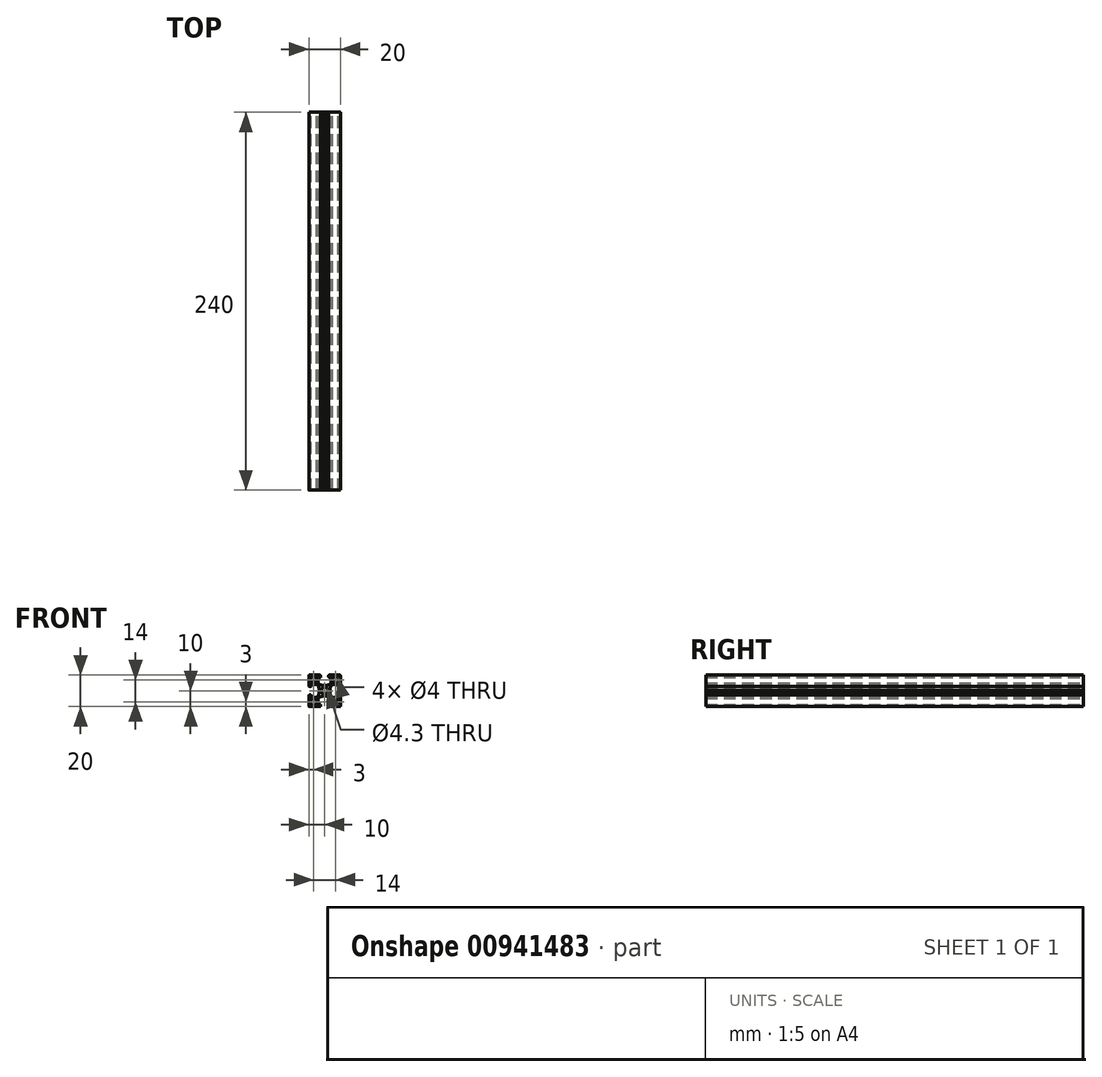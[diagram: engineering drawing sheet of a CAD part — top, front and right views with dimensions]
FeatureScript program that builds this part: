
annotation { "Feature Type Name" : "Feature", "Feature Type Description" : "" }
export const myFeature = defineFeature(function(context is Context, id is Id, definition is map)
    precondition{}
    {
        {
            var Q0;
            Q0=qCreatedBy(makeId("Front.planeOp"),FACE);
            var sketch = newSketch(context, id + "F0", { "sketchPlane" : qUnion([Q0])});
            skLineSegment(sketch, "E0", {"start": v(-11.2, 0) * mm, "end": v(11.2, 0) * mm});
            skCircle(sketch, "E1", {"center": v(0, 0) * mm, "radius": 2.15 * mm});
            skLineSegment(sketch, "E2", {"start": v(4.15, 4.94) * mm, "end": v(4.15, 8.2) * mm});
            skArc(sketch, "E3", {"start": v(4.15, 8.2) * mm, "mid": v(4.06, 8.41) * mm, "end": v(3.85, 8.5) * mm});
            skLineSegment(sketch, "E4", {"start": v(3.85, 8.5) * mm, "end": v(2.95, 8.5) * mm});
            skArc(sketch, "E5", {"start": v(2.95, 8.5) * mm, "mid": v(2.74, 8.59) * mm, "end": v(2.65, 8.8) * mm});
            skLineSegment(sketch, "E6", {"start": v(2.65, 8.8) * mm, "end": v(2.65, 9.7) * mm});
            skArc(sketch, "E7", {"start": v(2.65, 9.7) * mm, "mid": v(2.74, 9.91) * mm, "end": v(2.95, 10) * mm});
            skLineSegment(sketch, "E8", {"start": v(2.95, 10) * mm, "end": v(9.7, 10) * mm});
            skArc(sketch, "E9", {"start": v(9.7, 10) * mm, "mid": v(9.91, 9.91) * mm, "end": v(10, 9.7) * mm});
            skLineSegment(sketch, "E10", {"start": v(10, 9.7) * mm, "end": v(10, 2.95) * mm});
            skArc(sketch, "E11", {"start": v(10, 2.95) * mm, "mid": v(9.91, 2.74) * mm, "end": v(9.7, 2.65) * mm});
            skLineSegment(sketch, "E12", {"start": v(9.7, 2.65) * mm, "end": v(8.8, 2.65) * mm});
            skArc(sketch, "E13", {"start": v(8.8, 2.65) * mm, "mid": v(8.59, 2.74) * mm, "end": v(8.5, 2.95) * mm});
            skLineSegment(sketch, "E14", {"start": v(8.5, 2.95) * mm, "end": v(8.5, 3.85) * mm});
            skArc(sketch, "E15", {"start": v(8.5, 3.85) * mm, "mid": v(8.41, 4.06) * mm, "end": v(8.2, 4.15) * mm});
            skLineSegment(sketch, "E16", {"start": v(8.2, 4.15) * mm, "end": v(4.94, 4.15) * mm});
            skArc(sketch, "E17", {"start": v(4.94, 4.15) * mm, "mid": v(4.81, 4.12) * mm, "end": v(4.7, 4.04) * mm});
            skArc(sketch, "E18", {"start": v(4.7, 4.04) * mm, "mid": v(3.71, 2.28) * mm, "end": v(3.3, 0.3) * mm});
            skLineSegment(sketch, "E19", {"start": v(3.3, 0.3) * mm, "end": v(3, 0) * mm});
            skLineSegment(sketch, "E20", {"start": v(3, 0) * mm, "end": v(3.3, -0.3) * mm});
            skArc(sketch, "E21", {"start": v(3.3, -0.3) * mm, "mid": v(3.71, -2.28) * mm, "end": v(4.7, -4.04) * mm});
            skArc(sketch, "E22", {"start": v(4.7, -4.04) * mm, "mid": v(4.81, -4.12) * mm, "end": v(4.94, -4.15) * mm});
            skLineSegment(sketch, "E23", {"start": v(4.94, -4.15) * mm, "end": v(8.2, -4.15) * mm});
            skArc(sketch, "E24", {"start": v(8.2, -4.15) * mm, "mid": v(8.41, -4.06) * mm, "end": v(8.5, -3.85) * mm});
            skLineSegment(sketch, "E25", {"start": v(8.5, -3.85) * mm, "end": v(8.5, -2.95) * mm});
            skArc(sketch, "E26", {"start": v(8.5, -2.95) * mm, "mid": v(8.59, -2.74) * mm, "end": v(8.8, -2.65) * mm});
            skLineSegment(sketch, "E27", {"start": v(8.8, -2.65) * mm, "end": v(9.7, -2.65) * mm});
            skArc(sketch, "E28", {"start": v(9.7, -2.65) * mm, "mid": v(9.91, -2.74) * mm, "end": v(10, -2.95) * mm});
            skLineSegment(sketch, "E29", {"start": v(10, -2.95) * mm, "end": v(10, -9.7) * mm});
            skArc(sketch, "E30", {"start": v(10, -9.7) * mm, "mid": v(9.91, -9.91) * mm, "end": v(9.7, -10) * mm});
            skLineSegment(sketch, "E31", {"start": v(9.7, -10) * mm, "end": v(2.95, -10) * mm});
            skArc(sketch, "E32", {"start": v(2.95, -10) * mm, "mid": v(2.74, -9.91) * mm, "end": v(2.65, -9.7) * mm});
            skLineSegment(sketch, "E33", {"start": v(2.65, -9.7) * mm, "end": v(2.65, -8.8) * mm});
            skArc(sketch, "E34", {"start": v(2.65, -8.8) * mm, "mid": v(2.74, -8.59) * mm, "end": v(2.95, -8.5) * mm});
            skLineSegment(sketch, "E35", {"start": v(2.95, -8.5) * mm, "end": v(3.85, -8.5) * mm});
            skArc(sketch, "E36", {"start": v(3.85, -8.5) * mm, "mid": v(4.06, -8.41) * mm, "end": v(4.15, -8.2) * mm});
            skLineSegment(sketch, "E37", {"start": v(4.15, -8.2) * mm, "end": v(4.15, -4.94) * mm});
            skArc(sketch, "E38", {"start": v(4.15, -4.94) * mm, "mid": v(4.12, -4.81) * mm, "end": v(4.04, -4.7) * mm});
            skArc(sketch, "E39", {"start": v(4.04, -4.7) * mm, "mid": v(2.28, -3.71) * mm, "end": v(0.3, -3.3) * mm});
            skLineSegment(sketch, "E40", {"start": v(0.3, -3.3) * mm, "end": v(0, -3) * mm});
            skLineSegment(sketch, "E41", {"start": v(0, -3) * mm, "end": v(-0.3, -3.3) * mm});
            skArc(sketch, "E42", {"start": v(-0.3, -3.3) * mm, "mid": v(-2.28, -3.71) * mm, "end": v(-4.04, -4.7) * mm});
            skArc(sketch, "E43", {"start": v(-4.04, -4.7) * mm, "mid": v(-4.12, -4.81) * mm, "end": v(-4.15, -4.94) * mm});
            skLineSegment(sketch, "E44", {"start": v(-4.15, -4.94) * mm, "end": v(-4.15, -8.2) * mm});
            skArc(sketch, "E45", {"start": v(-4.15, -8.2) * mm, "mid": v(-4.06, -8.41) * mm, "end": v(-3.85, -8.5) * mm});
            skLineSegment(sketch, "E46", {"start": v(-3.85, -8.5) * mm, "end": v(-2.95, -8.5) * mm});
            skArc(sketch, "E47", {"start": v(-2.95, -8.5) * mm, "mid": v(-2.74, -8.59) * mm, "end": v(-2.65, -8.8) * mm});
            skLineSegment(sketch, "E48", {"start": v(-2.65, -8.8) * mm, "end": v(-2.65, -9.7) * mm});
            skArc(sketch, "E49", {"start": v(-2.65, -9.7) * mm, "mid": v(-2.74, -9.91) * mm, "end": v(-2.95, -10) * mm});
            skLineSegment(sketch, "E50", {"start": v(-2.95, -10) * mm, "end": v(-9.7, -10) * mm});
            skArc(sketch, "E51", {"start": v(-9.7, -10) * mm, "mid": v(-9.91, -9.91) * mm, "end": v(-10, -9.7) * mm});
            skLineSegment(sketch, "E52", {"start": v(-10, -9.7) * mm, "end": v(-10, -2.95) * mm});
            skArc(sketch, "E53", {"start": v(-10, -2.95) * mm, "mid": v(-9.91, -2.74) * mm, "end": v(-9.7, -2.65) * mm});
            skLineSegment(sketch, "E54", {"start": v(-9.7, -2.65) * mm, "end": v(-8.8, -2.65) * mm});
            skArc(sketch, "E55", {"start": v(-8.8, -2.65) * mm, "mid": v(-8.59, -2.74) * mm, "end": v(-8.5, -2.95) * mm});
            skLineSegment(sketch, "E56", {"start": v(-8.5, -2.95) * mm, "end": v(-8.5, -3.85) * mm});
            skArc(sketch, "E57", {"start": v(-8.5, -3.85) * mm, "mid": v(-8.41, -4.06) * mm, "end": v(-8.2, -4.15) * mm});
            skLineSegment(sketch, "E58", {"start": v(-8.2, -4.15) * mm, "end": v(-4.94, -4.15) * mm});
            skArc(sketch, "E59", {"start": v(-4.94, -4.15) * mm, "mid": v(-4.81, -4.12) * mm, "end": v(-4.7, -4.04) * mm});
            skArc(sketch, "E60", {"start": v(-4.7, -4.04) * mm, "mid": v(-3.71, -2.28) * mm, "end": v(-3.3, -0.3) * mm});
            skLineSegment(sketch, "E61", {"start": v(-3.3, -0.3) * mm, "end": v(-3, 0) * mm});
            skLineSegment(sketch, "E62", {"start": v(-3, 0) * mm, "end": v(-3.3, 0.3) * mm});
            skArc(sketch, "E63", {"start": v(-3.3, 0.3) * mm, "mid": v(-3.71, 2.28) * mm, "end": v(-4.7, 4.04) * mm});
            skArc(sketch, "E64", {"start": v(-4.7, 4.04) * mm, "mid": v(-4.81, 4.12) * mm, "end": v(-4.94, 4.15) * mm});
            skLineSegment(sketch, "E65", {"start": v(-4.94, 4.15) * mm, "end": v(-8.2, 4.15) * mm});
            skArc(sketch, "E66", {"start": v(-8.2, 4.15) * mm, "mid": v(-8.41, 4.06) * mm, "end": v(-8.5, 3.85) * mm});
            skLineSegment(sketch, "E67", {"start": v(-8.5, 3.85) * mm, "end": v(-8.5, 2.95) * mm});
            skArc(sketch, "E68", {"start": v(-8.5, 2.95) * mm, "mid": v(-8.59, 2.74) * mm, "end": v(-8.8, 2.65) * mm});
            skLineSegment(sketch, "E69", {"start": v(-8.8, 2.65) * mm, "end": v(-9.7, 2.65) * mm});
            skArc(sketch, "E70", {"start": v(-9.7, 2.65) * mm, "mid": v(-9.91, 2.74) * mm, "end": v(-10, 2.95) * mm});
            skLineSegment(sketch, "E71", {"start": v(-10, 2.95) * mm, "end": v(-10, 9.7) * mm});
            skArc(sketch, "E72", {"start": v(-10, 9.7) * mm, "mid": v(-9.91, 9.91) * mm, "end": v(-9.7, 10) * mm});
            skLineSegment(sketch, "E73", {"start": v(-9.7, 10) * mm, "end": v(-2.95, 10) * mm});
            skArc(sketch, "E74", {"start": v(-2.95, 10) * mm, "mid": v(-2.74, 9.91) * mm, "end": v(-2.65, 9.7) * mm});
            skLineSegment(sketch, "E75", {"start": v(-2.65, 9.7) * mm, "end": v(-2.65, 8.8) * mm});
            skArc(sketch, "E76", {"start": v(-2.65, 8.8) * mm, "mid": v(-2.74, 8.59) * mm, "end": v(-2.95, 8.5) * mm});
            skLineSegment(sketch, "E77", {"start": v(-2.95, 8.5) * mm, "end": v(-3.85, 8.5) * mm});
            skArc(sketch, "E78", {"start": v(-3.85, 8.5) * mm, "mid": v(-4.06, 8.41) * mm, "end": v(-4.15, 8.2) * mm});
            skLineSegment(sketch, "E79", {"start": v(-4.15, 8.2) * mm, "end": v(-4.15, 4.94) * mm});
            skArc(sketch, "E80", {"start": v(-4.15, 4.94) * mm, "mid": v(-4.12, 4.81) * mm, "end": v(-4.04, 4.7) * mm});
            skArc(sketch, "E81", {"start": v(-4.04, 4.7) * mm, "mid": v(-2.28, 3.71) * mm, "end": v(-0.3, 3.3) * mm});
            skLineSegment(sketch, "E82", {"start": v(-0.3, 3.3) * mm, "end": v(0, 3) * mm});
            skLineSegment(sketch, "E83", {"start": v(0, 3) * mm, "end": v(0.3, 3.3) * mm});
            skArc(sketch, "E84", {"start": v(0.3, 3.3) * mm, "mid": v(2.28, 3.71) * mm, "end": v(4.04, 4.7) * mm});
            skArc(sketch, "E85", {"start": v(4.04, 4.7) * mm, "mid": v(4.12, 4.81) * mm, "end": v(4.15, 4.94) * mm});
            skLineSegment(sketch, "E86", {"start": v(-9.5, 7) * mm, "end": v(-4.5, 7) * mm});
            skLineSegment(sketch, "E87", {"start": v(-7, 9.5) * mm, "end": v(-7, 4.5) * mm});
            skCircle(sketch, "E88", {"center": v(-7, 7) * mm, "radius": 2 * mm});
            skLineSegment(sketch, "E89", {"start": v(-9.5, -7) * mm, "end": v(-4.5, -7) * mm});
            skLineSegment(sketch, "E90", {"start": v(-7, -9.5) * mm, "end": v(-7, -4.5) * mm});
            skCircle(sketch, "E91", {"center": v(-7, -7) * mm, "radius": 2 * mm});
            skLineSegment(sketch, "E92", {"start": v(0, 11.2) * mm, "end": v(0, -11.2) * mm});
            skLineSegment(sketch, "E93", {"start": v(9.5, 7) * mm, "end": v(4.5, 7) * mm});
            skLineSegment(sketch, "E94", {"start": v(7, 9.5) * mm, "end": v(7, 4.5) * mm});
            skCircle(sketch, "E95", {"center": v(7, 7) * mm, "radius": 2 * mm});
            skCircle(sketch, "E96", {"center": v(7, -7) * mm, "radius": 2 * mm});
            skLineSegment(sketch, "E97", {"start": v(7, -9.5) * mm, "end": v(7, -4.5) * mm});
            skLineSegment(sketch, "E98", {"start": v(9.5, -7) * mm, "end": v(4.5, -7) * mm});
            skSolve(sketch);
        }
        {
            var Q0;
            Q0=makeQuery(id+"F0.imprint","IMPRINT",FACE,{"disambiguationData":[TD([[makeQuery(id+"F0.imprint","IMPRINT",EDGE,{"derivedFrom":sQuery(id+"F0.wireOp",EDGE,"E2")}),-1.0]])]});
            var Q1;
            {var subQ10=sQuery(id+"F0.wireOp",EDGE,"E20");Q1=makeQuery(id+"F0.imprint","IMPRINT",FACE,{"disambiguationData":[TD([[makeQuery(id+"F0.imprint","IMPRINT",EDGE,{"derivedFrom":subQ10}),-1.0]])]});}
            var Q2;
            {var subQ0=sQuery(id+"F0.wireOp",EDGE,"E62");Q2=makeQuery(id+"F0.imprint","IMPRINT",FACE,{"disambiguationData":[TD([[makeQuery(id+"F0.imprint","IMPRINT",EDGE,{"derivedFrom":subQ0}),-1.0]])]});}
            var Q3;
            {var subQ1=sQuery(id+"F0.wireOp",EDGE,"E41");Q3=makeQuery(id+"F0.imprint","IMPRINT",FACE,{"disambiguationData":[TD([[makeQuery(id+"F0.imprint","IMPRINT",EDGE,{"derivedFrom":subQ1}),-1.0]])]});}
            extrude(context, id + "F1", {"entities" : qUnion([Q0, Q1, Q2, Q3]), "depth" : 240 * mm, "offsetDistance" : 25 * mm});
        }
    });
